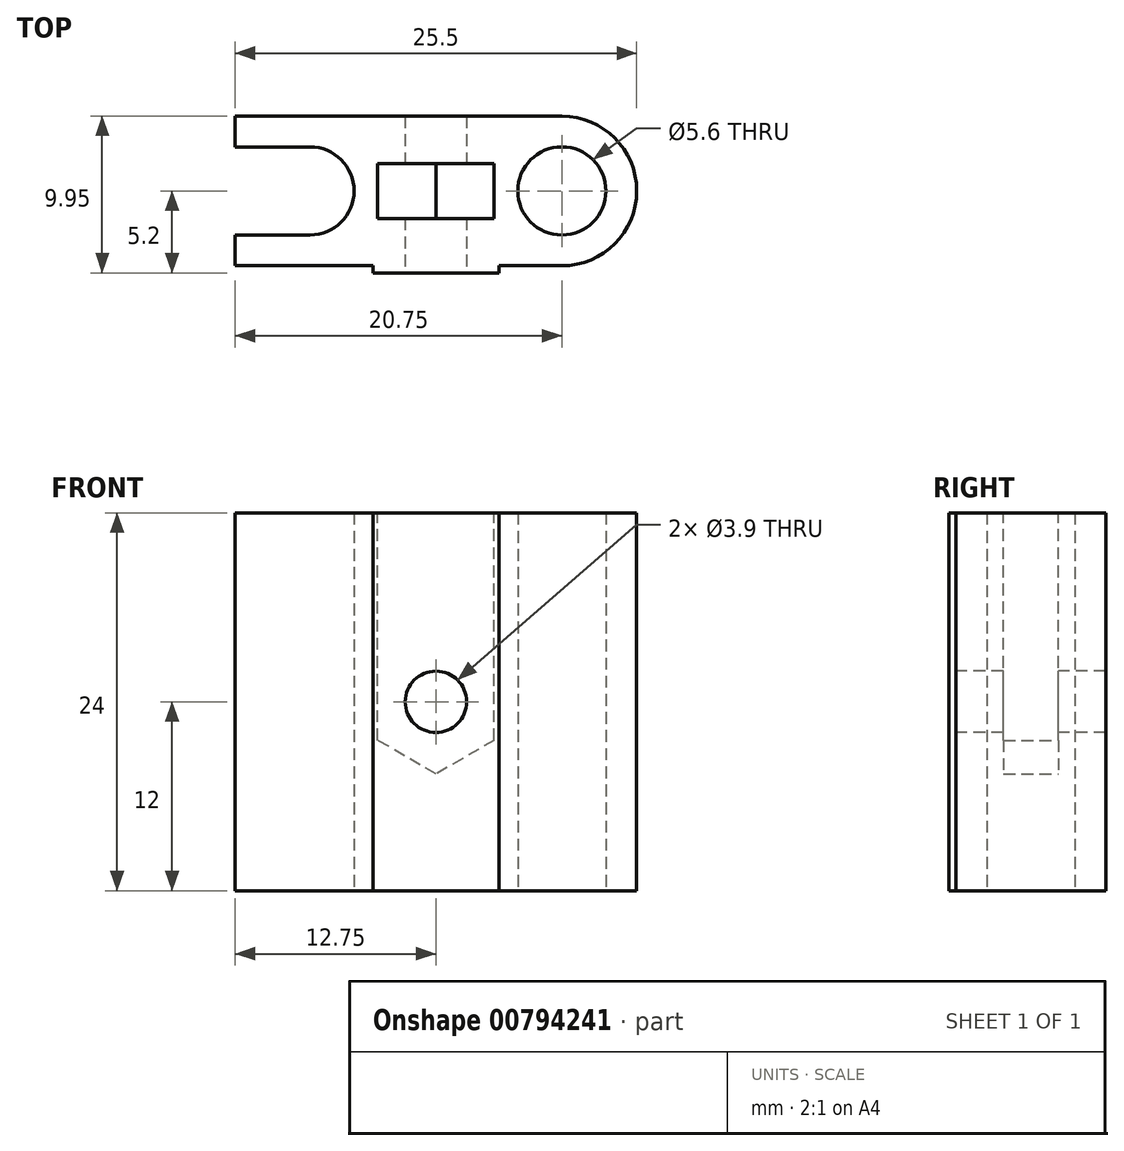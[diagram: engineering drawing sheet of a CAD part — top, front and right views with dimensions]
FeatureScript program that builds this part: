
annotation { "Feature Type Name" : "Feature", "Feature Type Description" : "" }
export const myFeature = defineFeature(function(context is Context, id is Id, definition is map)
    precondition{}
    {
        {
            var Q0;
            Q0=qCreatedBy(makeId("Top.planeOp"),FACE);
            var sketch = newSketch(context, id + "F0", { "sketchPlane" : qUnion([Q0])});
            skLineSegment(sketch, "E0", {"start": v(-8, 0) * mm, "end": v(8, 0) * mm, "construction": true});
            skArc(sketch, "E1", {"start": v(-8, -2.8) * mm, "mid": v(-5.2, 0) * mm, "end": v(-8, 2.8) * mm});
            skLineSegment(sketch, "E2", {"start": v(0, 21.05) * mm, "end": v(0, -24.42) * mm, "construction": true});
            skCircle(sketch, "E3.MirrorC", {"center": v(8, 0) * mm, "radius": 2.8 * mm});
            skLineSegment(sketch, "E4.bottom", {"start": v(8, 4.75) * mm, "end": v(-8, 4.75) * mm});
            skLineSegment(sketch, "E4.top", {"start": v(8, -4.75) * mm, "end": v(-8, -4.75) * mm});
            skLineSegment(sketch, "E4.left", {"start": v(8, 4.75) * mm, "end": v(8, -4.75) * mm, "construction": true});
            skPoint(sketch, "E4.middle", {"position": v(0, 0) * mm});
            skArc(sketch, "E5.0", {"start": v(8, 4.75) * mm, "mid": v(12.75, 0) * mm, "end": v(8, -4.75) * mm});
            skLineSegment(sketch, "E6.bottom", {"start": v(-8, 4.75) * mm, "end": v(-12.75, 4.75) * mm});
            skLineSegment(sketch, "E6.top", {"start": v(-8, -4.75) * mm, "end": v(-12.75, -4.75) * mm});
            skLineSegment(sketch, "E6.left", {"start": v(-8, 4.75) * mm, "end": v(-8, -4.75) * mm, "construction": true});
            skLineSegment(sketch, "E6.right", {"start": v(-12.75, 4.75) * mm, "end": v(-12.75, 2.8) * mm});
            skLineSegment(sketch, "E7", {"start": v(-8, 2.8) * mm, "end": v(-12.75, 2.8) * mm});
            skLineSegment(sketch, "E8", {"start": v(-8, -2.8) * mm, "end": v(-12.75, -2.8) * mm});
            skLineSegment(sketch, "E9.trimOffspring", {"start": v(-12.75, -2.8) * mm, "end": v(-12.75, -4.75) * mm});
            skLineSegment(sketch, "E10.bottom", {"start": v(4, -4.3) * mm, "end": v(-4, -4.3) * mm});
            skLineSegment(sketch, "E10.top", {"start": v(4, -5.2) * mm, "end": v(-4, -5.2) * mm});
            skLineSegment(sketch, "E10.left", {"start": v(4, -4.3) * mm, "end": v(4, -5.2) * mm});
            skLineSegment(sketch, "E10.right", {"start": v(-4, -4.3) * mm, "end": v(-4, -5.2) * mm});
            skPoint(sketch, "E10.middle", {"position": v(0, -4.75) * mm});
            skSolve(sketch);
        }
        {
            var Q0;
            Q0 = qSketchRegion(id + "F0", true);
            var Q1;
            Q1 = qSketchRegion(id + "F2", true);
            extrude(context, id + "F1", {"entities" : qUnion([Q0, Q1]), "depth" : 24 * mm, "offsetDistance" : 25 * mm});
        }
        {
            var Q0;
            Q0=makeQuery(id+"F1.opExtrude","SWEPT_FACE",FACE,{"disambiguationData":[OSD([sQuery(id+"F0.wireOp",EDGE,"E10.top")])]});
            var sketch = newSketch(context, id + "F2", { "sketchPlane" : qUnion([Q0])});
            skLineSegment(sketch, "E11.bottom", {"start": v(-4, 24) * mm, "end": v(4, 24) * mm, "construction": true});
            skLineSegment(sketch, "E11.top", {"start": v(-4, 0) * mm, "end": v(4, 0) * mm, "construction": true});
            skLineSegment(sketch, "E11.left", {"start": v(-4, 24) * mm, "end": v(-4, 0) * mm, "construction": true});
            skLineSegment(sketch, "E11.right", {"start": v(4, 24) * mm, "end": v(4, 0) * mm, "construction": true});
            skLineSegment(sketch, "E12", {"start": v(-4, 24) * mm, "end": v(4, 0) * mm, "construction": true});
            skLineSegment(sketch, "E13", {"start": v(0, 0) * mm, "end": v(0, 24) * mm, "construction": true});
            skCircle(sketch, "E14", {"center": v(0, 12) * mm, "radius": 1.95 * mm});
            skSolve(sketch);
        }
        {
            var Q0;
            Q0 = qSketchRegion(id + "F2", true);
            extrude(context, id + "F3", {"entities" : qUnion([Q0]), "operationType" : NewBodyOperationType.REMOVE, "endBound" : BoundingType.THROUGH_ALL, "oppositeDirection" : true, "depth" : 25 * mm, "offsetDistance" : 25 * mm});
        }
        {
            var Q0;
            Q0=makeQuery(id+"F1.opExtrude","CAP_FACE",FACE,{"disambiguationData":[OSD([sQuery(id+"F0.wireOp",EDGE,"E1"),sQuery(id+"F0.wireOp",EDGE,"E3.MirrorC"),sQuery(id+"F0.wireOp",EDGE,"E4.bottom"),sQuery(id+"F0.wireOp",EDGE,"E4.top"),sQuery(id+"F0.wireOp",EDGE,"E5.0"),sQuery(id+"F0.wireOp",EDGE,"E6.bottom"),sQuery(id+"F0.wireOp",EDGE,"E6.top"),sQuery(id+"F0.wireOp",EDGE,"E6.right"),sQuery(id+"F0.wireOp",EDGE,"E7"),sQuery(id+"F0.wireOp",EDGE,"E8"),sQuery(id+"F0.wireOp",EDGE,"E9.trimOffspring"),sQuery(id+"F0.wireOp",EDGE,"E10.top"),sQuery(id+"F0.wireOp",EDGE,"E10.left"),sQuery(id+"F0.wireOp",EDGE,"E10.right")])],"isStart":false});
            var sketch = newSketch(context, id + "F4", { "sketchPlane" : qUnion([Q0])});
            skLineSegment(sketch, "E15.bottom", {"start": v(-3.7, -1.75) * mm, "end": v(3.7, -1.75) * mm});
            skLineSegment(sketch, "E15.top", {"start": v(-3.7, 1.75) * mm, "end": v(3.7, 1.75) * mm});
            skLineSegment(sketch, "E15.left", {"start": v(-3.7, -1.75) * mm, "end": v(-3.7, 1.75) * mm});
            skLineSegment(sketch, "E15.right", {"start": v(3.7, -1.75) * mm, "end": v(3.7, 1.75) * mm});
            skPoint(sketch, "E15.middle", {"position": v(0, 0) * mm});
            skSolve(sketch);
        }
        {
            var Q0;
            Q0=makeQuery(id+"F4.imprint","IMPRINT",FACE,{"disambiguationData":[TD([[makeQuery(id+"F4.imprint","IMPRINT",EDGE,{"derivedFrom":sQuery(id+"F4.wireOp",EDGE,"E15.bottom")}),1.0]])]});
            extrude(context, id + "F5", {"entities" : qUnion([Q0]), "operationType" : NewBodyOperationType.REMOVE, "oppositeDirection" : true, "depth" : 12 * mm, "offsetDistance" : 25 * mm});
        }
        {
            var Q0;
            Q0=makeQuery(id+"F5.boolean.opBoolean","COPY",FACE,{"derivedFrom":makeQuery(id+"F5.opExtrude","SWEPT_FACE",FACE,{"disambiguationData":[OSD([sQuery(id+"F4.wireOp",EDGE,"E15.top")])]})});
            var sketch = newSketch(context, id + "F6", { "sketchPlane" : qUnion([Q0])});
            skLineSegment(sketch, "E16.bottom", {"start": v(-3.7, 24) * mm, "end": v(3.7, 24) * mm, "construction": true});
            skLineSegment(sketch, "E16.top", {"start": v(-3.7, 12) * mm, "end": v(3.7, 12) * mm, "construction": true});
            skLineSegment(sketch, "E16.left", {"start": v(-3.7, 24) * mm, "end": v(-3.7, 12) * mm, "construction": true});
            skLineSegment(sketch, "E16.right", {"start": v(3.7, 24) * mm, "end": v(3.7, 12) * mm, "construction": true});
            skLineSegment(sketch, "E17", {"start": v(-3.7, 11.7) * mm, "end": v(3.7, 11.7) * mm, "construction": true});
            skCircle(sketch, "E18.cCircle", {"center": v(0, 11.7) * mm, "radius": 3.7 * mm, "construction": true});
            skLineSegment(sketch, "E18.0", {"start": v(3.7, 13.84) * mm, "end": v(3.7, 9.56) * mm});
            skLineSegment(sketch, "E18.1", {"start": v(3.7, 9.56) * mm, "end": v(0, 7.43) * mm});
            skLineSegment(sketch, "E18.2", {"start": v(0, 7.43) * mm, "end": v(-3.7, 9.56) * mm});
            skLineSegment(sketch, "E18.3", {"start": v(-3.7, 9.56) * mm, "end": v(-3.7, 13.84) * mm});
            skLineSegment(sketch, "E18.4", {"start": v(-3.7, 13.84) * mm, "end": v(0, 15.97) * mm});
            skLineSegment(sketch, "E18.5", {"start": v(0, 15.97) * mm, "end": v(3.7, 13.84) * mm});
            skPoint(sketch, "E18.0.midPoint", {"position": v(3.7, 11.7) * mm});
            skSolve(sketch);
        }
        {
            var Q0;
            Q0 = qSketchRegion(id + "F6", true);
            var Q1;
            {var subQ0=sQuery(id+"F4.wireOp",EDGE,"E15.bottom");Q1=makeQuery(id+"F5.boolean.opBoolean","INTERSECT",VERTEX,{"disambiguationData":[OD(1.0)],"derivedFrom":[makeQuery(id+"F3.boolean.opBoolean","COPY",FACE,{"derivedFrom":makeQuery(id+"F3.opExtrude","SWEPT_FACE",FACE,{"disambiguationData":[OSD([sQuery(id+"F2.wireOp",EDGE,"E14")])]})}),makeQuery(id+"F5.opExtrude","SWEPT_FACE",FACE,{"disambiguationData":[OSD([subQ0])]}),makeQuery(id+"F5.opExtrude","CAP_FACE",FACE,{"disambiguationData":[OSD([subQ0,sQuery(id+"F4.wireOp",EDGE,"E15.top"),sQuery(id+"F4.wireOp",EDGE,"E15.left"),sQuery(id+"F4.wireOp",EDGE,"E15.right")])],"isStart":false})]});}
            extrude(context, id + "F7", {"entities" : qUnion([Q0]), "operationType" : NewBodyOperationType.REMOVE, "endBound" : BoundingType.UP_TO_VERTEX, "depth" : 25 * mm, "endBoundEntityVertex" : qUnion([Q1]), "offsetDistance" : 25 * mm});
        }
    });
